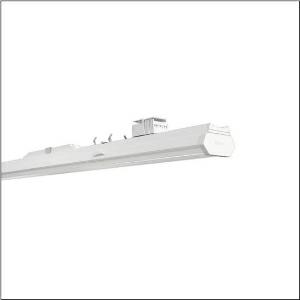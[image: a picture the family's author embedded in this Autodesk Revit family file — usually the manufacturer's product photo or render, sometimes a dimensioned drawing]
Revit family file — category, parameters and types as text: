
# Revit family: licross_r__21_protected_mo_52td1bvn455g_6e17
name_source: partatom
category: Lighting Fixtures
units: mm (PartAtom-declared; Revit-internal decimal feet)

## family parameters
Cut with Voids When Loaded = No
Host = Face
Light Source = No
Part Type = Normal
Room Calculation Point = No
Round Connector Dimension = Use Diameter
Shared = No

## types (1)
- --- (1 x LED, 5500 lm, 32.3 W, 4000K)
    Apparent Load = 32 VA
    CIE Flux Codes = 54 82 95 97 100
    Color Rendering = 80
    Color Temperature = 4000K
    Default Elevation = 1800 mm
    Description = Licross® 21 Protected MO, luminaire insert, of sheet steel, galvanised, coil coated, white, length: 1.500mm, width: 90mm, height: 101mm, LED rated luminous flux: 5.500lm, light colour: 840, control gear: DALI 2, CLO, with plug, 5-pole, with phase selection, mains connection: 220..240V, AC, 50/60Hz, start of lifetime: 32W, end of service life: 38W, internal wiring halogen-free, primary optical cover: cover, of PMMA, light emission: direct distribution, primary light characteristic: symmetric, protection rating (complete): IP54, insulation class (complete): insulation class I (protective earthing), certification: CE, ENEC, VDE, UKCA, protection symbol: D if used in an environment with non-conductive dust loads with corresponding accessories, impact resistance: IK06, permissible ambient temperature for indoor applications: -25..+45°C, corresponds to IFS (International Featured Standards) requirements for safety and quality in the food industry, reducing of maximum allowable ambient temperature of 5°C with ceiling mounting, LABS conformity tested according to VDMA 24364:2018-05, packaging unit: 1 piece
    Height = 92 mm
    Lamp = 1 x LED
    Lamp Light Flux = 5500 lm
    Lamp Power = 32.3 W
    Lamp count = 1
    Length = 1500 mm
    Luminous efficacy = 170 lm/W
    Manufacturer = Siteco
    ModVariant = No
    Model = 52TD1BVN455G
    Mounting Place = Ceiling
    Mounting Type = Pendant
    Number of Poles = 1
    OnlyDefault = Yes
    Power Factor = 1
    Product Name = Licross® 21 Protected MO
    Product group = luminaire insert | ceiling pendant
    ProductGroupID = 902
    Protection Class = Protection class I
    Protection Degree = IP 54
    RLX_Detail_Level = 1
    RLX_Emergency_Light_Flux = 0 lm
    RLX_Emergency_Type = 0
    RLX_Emergency_Type_DB = No
    RlxData = <blob elided: 24029 chars, md5=dd7e5430>
    Socket = socket
    Standby Power = 0 W
    System Light Flux = 5500 lm
    System Power = 32 W
    Type Comments = factory setting: luminous flux: 100 % | dim-lin: 254 | 219 mA
    Type Image = l_1256148.jpg
    URL = http://relux.com
    VarID = @adj_104301
    Voltage = 0 V
    Weight = 0.00 kg
    Width = 88 mm

## geometry (parser evidence)
native form markers: Blend x4, Sweep x9
no freeform markers — native parametric forms only
